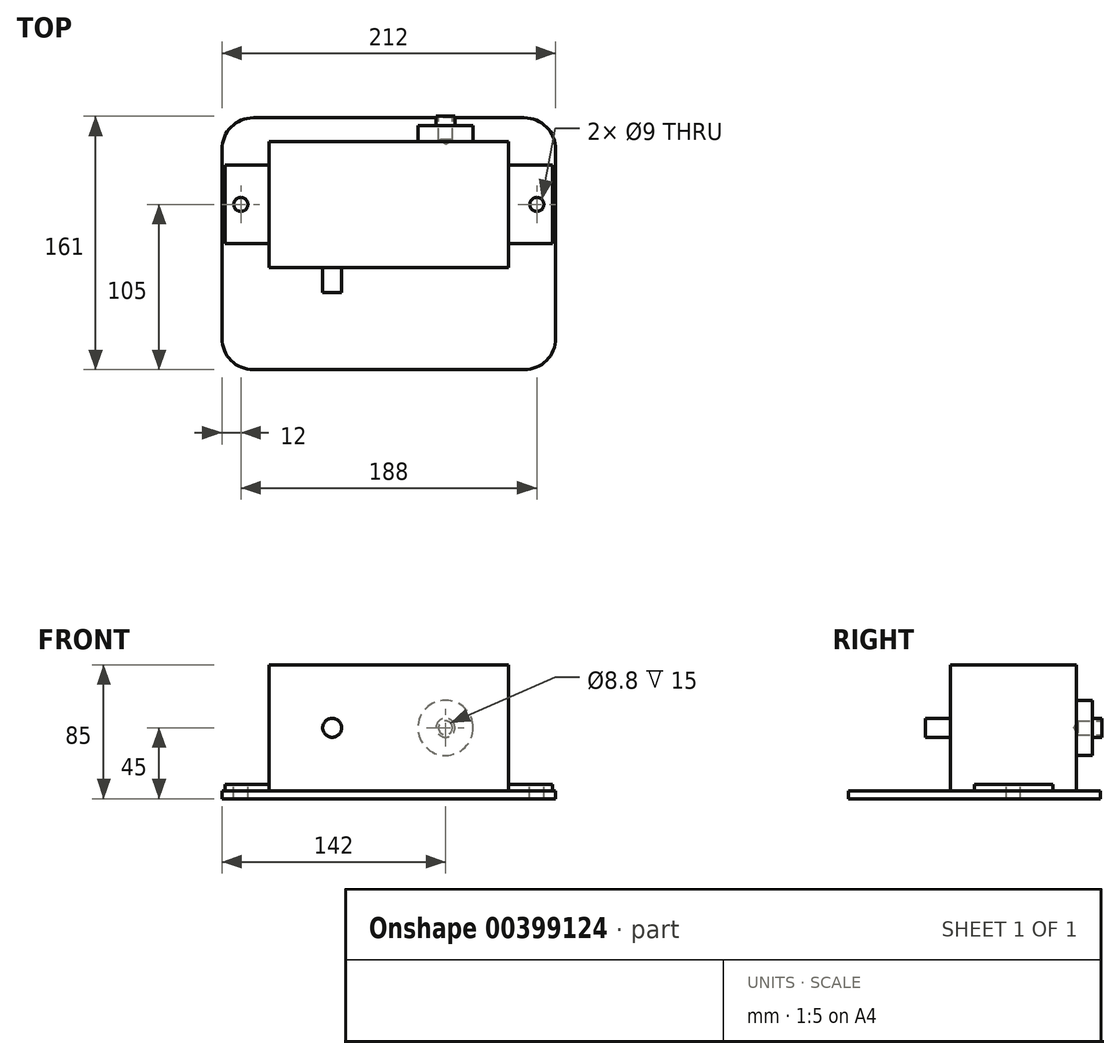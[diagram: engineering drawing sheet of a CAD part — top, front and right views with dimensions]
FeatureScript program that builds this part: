
annotation { "Feature Type Name" : "Feature", "Feature Type Description" : "" }
export const myFeature = defineFeature(function(context is Context, id is Id, definition is map)
    precondition{}
    {
        {
            var Q0;
            Q0=qCreatedBy(makeId("Top.planeOp"),FACE);
            var sketch = newSketch(context, id + "F0", { "sketchPlane" : qUnion([Q0])});
            skLineSegment(sketch, "E0.bottom", {"start": v(106, 80) * mm, "end": v(-106, 80) * mm});
            skLineSegment(sketch, "E0.top", {"start": v(106, -80) * mm, "end": v(-106, -80) * mm});
            skLineSegment(sketch, "E0.left", {"start": v(106, 80) * mm, "end": v(106, -80) * mm});
            skLineSegment(sketch, "E0.right", {"start": v(-106, 80) * mm, "end": v(-106, -80) * mm});
            skPoint(sketch, "E0.middle", {"position": v(0, 0) * mm});
            skSolve(sketch);
        }
        {
            var Q0;
            Q0=makeQuery(id+"F0.imprint","IMPRINT",FACE,{"disambiguationData":[TD([[makeQuery(id+"F0.imprint","IMPRINT",EDGE,{"derivedFrom":sQuery(id+"F0.wireOp",EDGE,"E0.bottom")}),1.0]])]});
            extrude(context, id + "F1", {"entities" : qUnion([Q0]), "depth" : 5 * mm});
        }
        {
            var Q0;
            Q0=makeQuery(id+"F1.opExtrude","CAP_FACE",FACE,{"disambiguationData":[OSD([sQuery(id+"F0.wireOp",EDGE,"E0.bottom"),sQuery(id+"F0.wireOp",EDGE,"E0.top"),sQuery(id+"F0.wireOp",EDGE,"E0.left"),sQuery(id+"F0.wireOp",EDGE,"E0.right")])],"isStart":false});
            var sketch = newSketch(context, id + "F2", { "sketchPlane" : qUnion([Q0])});
            skLineSegment(sketch, "E1.bottom", {"start": v(-76, 65) * mm, "end": v(76, 65) * mm});
            skLineSegment(sketch, "E1.top", {"start": v(-76, -15) * mm, "end": v(76, -15) * mm});
            skLineSegment(sketch, "E1.left", {"start": v(-76, 65) * mm, "end": v(-76, -15) * mm});
            skLineSegment(sketch, "E1.right", {"start": v(76, 65) * mm, "end": v(76, -15) * mm});
            skSolve(sketch);
        }
        {
            var Q0;
            Q0=makeQuery(id+"F2.imprint","IMPRINT",FACE,{"disambiguationData":[TD([[makeQuery(id+"F2.imprint","IMPRINT",EDGE,{"derivedFrom":sQuery(id+"F2.wireOp",EDGE,"E1.bottom")}),-1.0]])]});
            extrude(context, id + "F3", {"entities" : qUnion([Q0]), "operationType" : NewBodyOperationType.ADD, "depth" : 80 * mm});
        }
        {
            var Q0;
            Q0=makeQuery(id+"F3.opExtrude","SWEPT_FACE",FACE,{"disambiguationData":[OSD([sQuery(id+"F2.wireOp",EDGE,"E1.top")])]});
            var sketch = newSketch(context, id + "F4", { "sketchPlane" : qUnion([Q0])});
            skCircle(sketch, "E2", {"center": v(-36, 45) * mm, "radius": 6 * mm});
            skSolve(sketch);
        }
        {
            var Q0;
            Q0=makeQuery(id+"F4.imprint","IMPRINT",FACE,{"disambiguationData":[TD([[makeQuery(id+"F4.imprint","IMPRINT",EDGE,{"derivedFrom":sQuery(id+"F4.wireOp",EDGE,"E2")}),1.0]])]});
            extrude(context, id + "F5", {"entities" : qUnion([Q0]), "operationType" : NewBodyOperationType.ADD, "depth" : 16 * mm});
        }
        {
            var Q0;
            Q0=makeQuery(id+"F3.opExtrude","SWEPT_FACE",FACE,{"disambiguationData":[OSD([sQuery(id+"F2.wireOp",EDGE,"E1.bottom")])]});
            var sketch = newSketch(context, id + "F6", { "sketchPlane" : qUnion([Q0])});
            skCircle(sketch, "E3", {"center": v(-36, 45) * mm, "radius": 6 * mm});
            skSolve(sketch);
        }
        {
            var Q0;
            Q0=makeQuery(id+"F6.imprint","IMPRINT",FACE,{"disambiguationData":[TD([[makeQuery(id+"F6.imprint","IMPRINT",EDGE,{"derivedFrom":sQuery(id+"F6.wireOp",EDGE,"E3")}),1.0]])]});
            extrude(context, id + "F7", {"entities" : qUnion([Q0]), "operationType" : NewBodyOperationType.ADD, "depth" : 16 * mm});
        }
        {
            var Q0;
            Q0=makeQuery(id+"F7.opExtrude","CAP_FACE",FACE,{"disambiguationData":[OSD([sQuery(id+"F6.wireOp",EDGE,"E3")])],"isStart":false});
            var sketch = newSketch(context, id + "F8", { "sketchPlane" : qUnion([Q0])});
            skPoint(sketch, "E4", {"position": v(-36, 45) * mm});
            skSolve(sketch);
        }
        {
            var Q0;
            Q0=sQuery(id+"F8.wireOp",VERTEX,"E4");
            var Q1;
            Q1=makeQuery(id+"F1.opExtrude","SWEPT_BODY",BODY,{"disambiguationData":[OSD([sQuery(id+"F0.wireOp",EDGE,"E0.bottom"),sQuery(id+"F0.wireOp",EDGE,"E0.top"),sQuery(id+"F0.wireOp",EDGE,"E0.left"),sQuery(id+"F0.wireOp",EDGE,"E0.right")])]});
            hole(context, id + "F9", {"style" : HoleStyle.SIMPLE, "endStyle" : HoleEndStyle.BLIND, "standardTappedOrClearance" : lookupTablePath({ "standard" : "ISO", "fit" : "Normal", "size" : "M8", "type" : "Clearance" }), "standardBlindInLast" : lookupTablePath({ "fit" : "Standard", "standard" : "ISO", "size" : "M8", "type" : "Clearance" }), "holeDiameter" : 8.8 * mm, "holeDepth" : 15 * mm, "isTappedThrough" : true, "tappedDepth" : 12 * mm, "tapClearance" : 3, "locations" : qUnion([Q0]), "scope" : qUnion([Q1])});
        }
        {
            var Q0;
            Q0=makeQuery(id+"F1.opExtrude","SWEPT_EDGE",EDGE,{"disambiguationData":[OSD([sQuery(id+"F0.wireOp",EDGE,"E0.top"),sQuery(id+"F0.wireOp",EDGE,"E0.left")])]});
            var Q1;
            Q1=makeQuery(id+"F1.opExtrude","SWEPT_EDGE",EDGE,{"disambiguationData":[OSD([sQuery(id+"F0.wireOp",EDGE,"E0.bottom"),sQuery(id+"F0.wireOp",EDGE,"E0.left")])]});
            var Q2;
            Q2=makeQuery(id+"F1.opExtrude","SWEPT_EDGE",EDGE,{"disambiguationData":[OSD([sQuery(id+"F0.wireOp",EDGE,"E0.bottom"),sQuery(id+"F0.wireOp",EDGE,"E0.right")])]});
            var Q3;
            Q3=makeQuery(id+"F1.opExtrude","SWEPT_EDGE",EDGE,{"disambiguationData":[OSD([sQuery(id+"F0.wireOp",EDGE,"E0.top"),sQuery(id+"F0.wireOp",EDGE,"E0.right")])]});
            fillet(context, id + "F10", {"entities" : qUnion([Q0, Q1, Q2, Q3]), "radius" : 20 * mm, "tangentPropagation" : true, "allowEdgeOverflow" : false});
        }
        {
            var Q0;
            Q0=makeQuery(id+"F3.opExtrude","SWEPT_FACE",FACE,{"disambiguationData":[OSD([sQuery(id+"F2.wireOp",EDGE,"E1.bottom")])]});
            var sketch = newSketch(context, id + "F11", { "sketchPlane" : qUnion([Q0])});
            skCircle(sketch, "E5", {"center": v(-36, 45) * mm, "radius": 17.5 * mm});
            skSolve(sketch);
        }
        {
            var Q0;
            Q0=makeQuery(id+"F11.imprint","IMPRINT",FACE,{"disambiguationData":[TD([[makeQuery(id+"F11.imprint","IMPRINT",EDGE,{"derivedFrom":sQuery(id+"F11.wireOp",EDGE,"E5")}),1.0]])]});
            extrude(context, id + "F12", {"entities" : qUnion([Q0]), "operationType" : NewBodyOperationType.ADD, "depth" : 10 * mm});
        }
        {
            var Q0;
            Q0=makeQuery(id+"F1.opExtrude","CAP_FACE",FACE,{"disambiguationData":[OSD([sQuery(id+"F0.wireOp",EDGE,"E0.bottom"),sQuery(id+"F0.wireOp",EDGE,"E0.top"),sQuery(id+"F0.wireOp",EDGE,"E0.left"),sQuery(id+"F0.wireOp",EDGE,"E0.right")])],"isStart":false});
            var sketch = newSketch(context, id + "F13", { "sketchPlane" : qUnion([Q0])});
            skLineSegment(sketch, "E6.bottom", {"start": v(-76, 50) * mm, "end": v(-104, 50) * mm});
            skLineSegment(sketch, "E6.top", {"start": v(-76, 0) * mm, "end": v(-104, 0) * mm});
            skLineSegment(sketch, "E6.left", {"start": v(-76, 50) * mm, "end": v(-76, 0) * mm});
            skLineSegment(sketch, "E6.right", {"start": v(-104, 50) * mm, "end": v(-104, 0) * mm});
            skPoint(sketch, "E7.firstSnap0", {"position": v(76, 25) * mm});
            skLineSegment(sketch, "E7.bottom", {"start": v(76, 50) * mm, "end": v(104, 50) * mm});
            skLineSegment(sketch, "E7.top", {"start": v(76, 0) * mm, "end": v(104, 0) * mm});
            skLineSegment(sketch, "E7.left", {"start": v(76, 50) * mm, "end": v(76, 0) * mm});
            skLineSegment(sketch, "E7.right", {"start": v(104, 50) * mm, "end": v(104, 0) * mm});
            skSolve(sketch);
        }
        {
            var Q0;
            Q0=makeQuery(id+"F13.imprint","IMPRINT",FACE,{"disambiguationData":[TD([[makeQuery(id+"F13.imprint","IMPRINT",EDGE,{"derivedFrom":sQuery(id+"F13.wireOp",EDGE,"E6.bottom")}),1.0]])]});
            var Q1;
            Q1=makeQuery(id+"F13.imprint","IMPRINT",FACE,{"disambiguationData":[TD([[makeQuery(id+"F13.imprint","IMPRINT",EDGE,{"derivedFrom":sQuery(id+"F13.wireOp",EDGE,"E7.bottom")}),-1.0]])]});
            extrude(context, id + "F14", {"entities" : qUnion([Q0, Q1]), "operationType" : NewBodyOperationType.ADD, "depth" : 4 * mm});
        }
        {
            var Q0;
            Q0=makeQuery(id+"F14.opExtrude","CAP_FACE",FACE,{"disambiguationData":[OSD([sQuery(id+"F13.wireOp",EDGE,"E6.bottom"),sQuery(id+"F13.wireOp",EDGE,"E6.top"),sQuery(id+"F13.wireOp",EDGE,"E6.left"),sQuery(id+"F13.wireOp",EDGE,"E6.right")])],"isStart":false});
            var sketch = newSketch(context, id + "F15", { "sketchPlane" : qUnion([Q0])});
            skPoint(sketch, "E8", {"position": v(-94, 25) * mm});
            skPoint(sketch, "E8.positionSnap0", {"position": v(-104, 25) * mm});
            skPoint(sketch, "E9", {"position": v(94, 25) * mm});
            skPoint(sketch, "E9.positionSnap0", {"position": v(-76, 25) * mm});
            skSolve(sketch);
        }
        {
            var Q0;
            Q0=sQuery(id+"F15.wireOp",VERTEX,"E8");
            var Q1;
            Q1=sQuery(id+"F15.wireOp",VERTEX,"E9");
            var Q2;
            Q2=makeQuery(id+"F1.opExtrude","SWEPT_BODY",BODY,{"disambiguationData":[OSD([sQuery(id+"F0.wireOp",EDGE,"E0.bottom"),sQuery(id+"F0.wireOp",EDGE,"E0.top"),sQuery(id+"F0.wireOp",EDGE,"E0.left"),sQuery(id+"F0.wireOp",EDGE,"E0.right")])]});
            hole(context, id + "F16", {"style" : HoleStyle.SIMPLE, "endStyle" : HoleEndStyle.BLIND, "holeDiameter" : 9 * mm, "holeDepth" : 15 * mm, "isTappedThrough" : true, "tappedDepth" : 12 * mm, "tapClearance" : 3, "locations" : qUnion([Q0, Q1]), "scope" : qUnion([Q2])});
        }
    });
